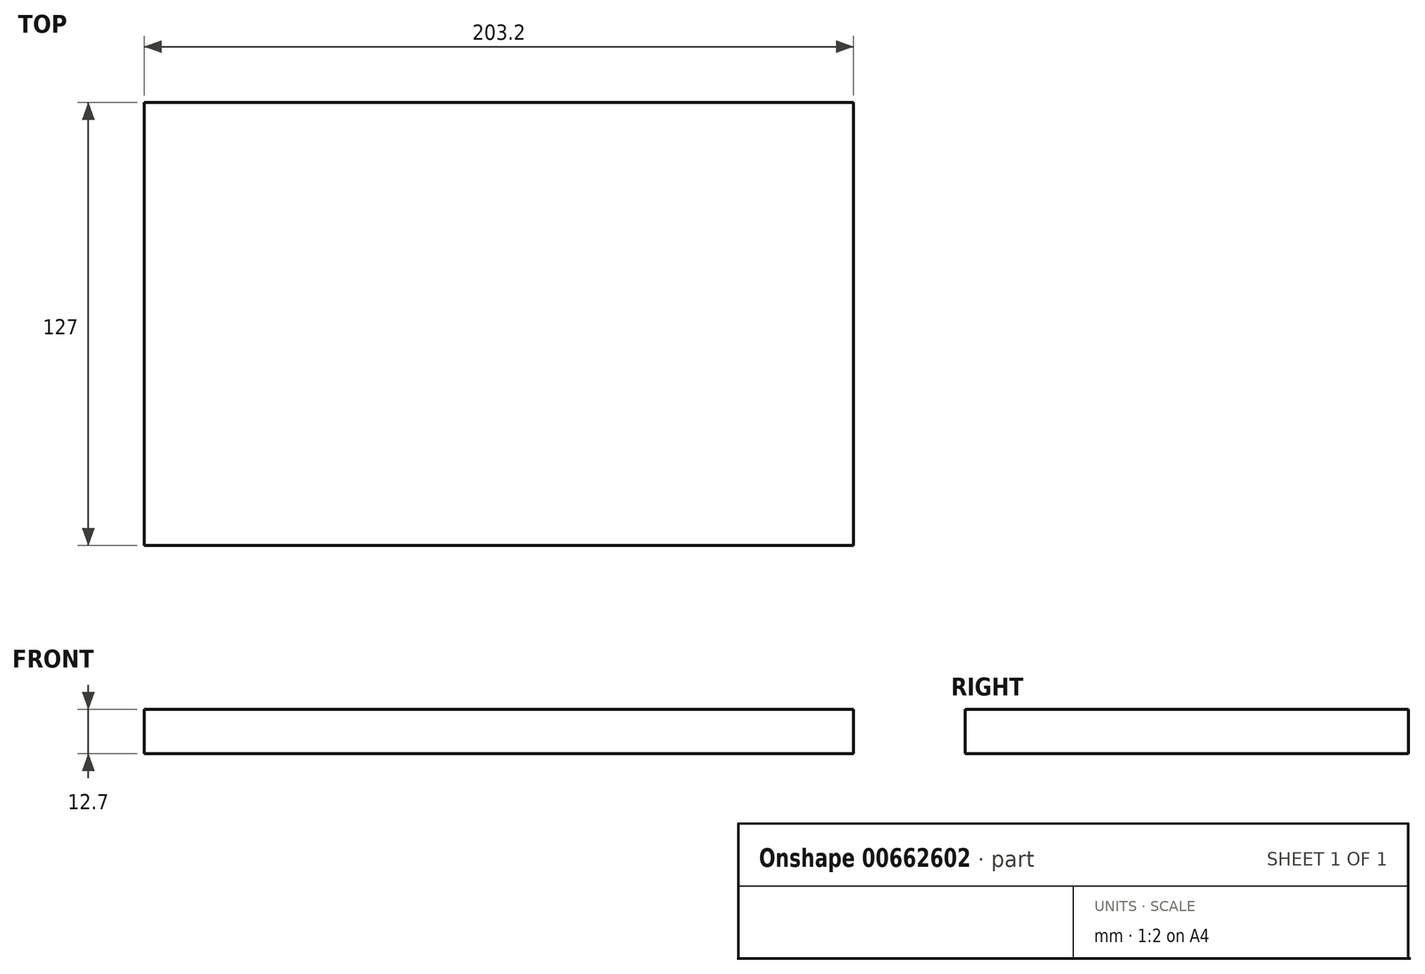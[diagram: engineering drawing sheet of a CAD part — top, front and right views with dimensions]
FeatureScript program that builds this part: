
annotation { "Feature Type Name" : "Feature", "Feature Type Description" : "" }
export const myFeature = defineFeature(function(context is Context, id is Id, definition is map)
    precondition{}
    {
        {
            var Q0;
            Q0=qCreatedBy(makeId("Top.planeOp"),FACE);
            var sketch = newSketch(context, id + "F0", { "sketchPlane" : qUnion([Q0])});
            skLineSegment(sketch, "E0.bottom", {"start": v(101.6, 63.5) * mm, "end": v(-101.6, 63.5) * mm});
            skLineSegment(sketch, "E0.top", {"start": v(101.6, -63.5) * mm, "end": v(-101.6, -63.5) * mm});
            skLineSegment(sketch, "E0.left", {"start": v(101.6, 63.5) * mm, "end": v(101.6, -63.5) * mm});
            skLineSegment(sketch, "E0.right", {"start": v(-101.6, 63.5) * mm, "end": v(-101.6, -63.5) * mm});
            skPoint(sketch, "E0.middle", {"position": v(0, 0) * mm});
            skSolve(sketch);
        }
        {
            var Q0;
            Q0=makeQuery(id+"F0.imprint","IMPRINT",FACE,{"disambiguationData":[TD([[makeQuery(id+"F0.imprint","IMPRINT",EDGE,{"derivedFrom":sQuery(id+"F0.wireOp",EDGE,"E0.bottom")}),1.0]])]});
            extrude(context, id + "F1", {"entities" : qUnion([Q0]), "depth" : 12.7 * mm, "offsetDistance" : 25.4 * mm});
        }
    });
